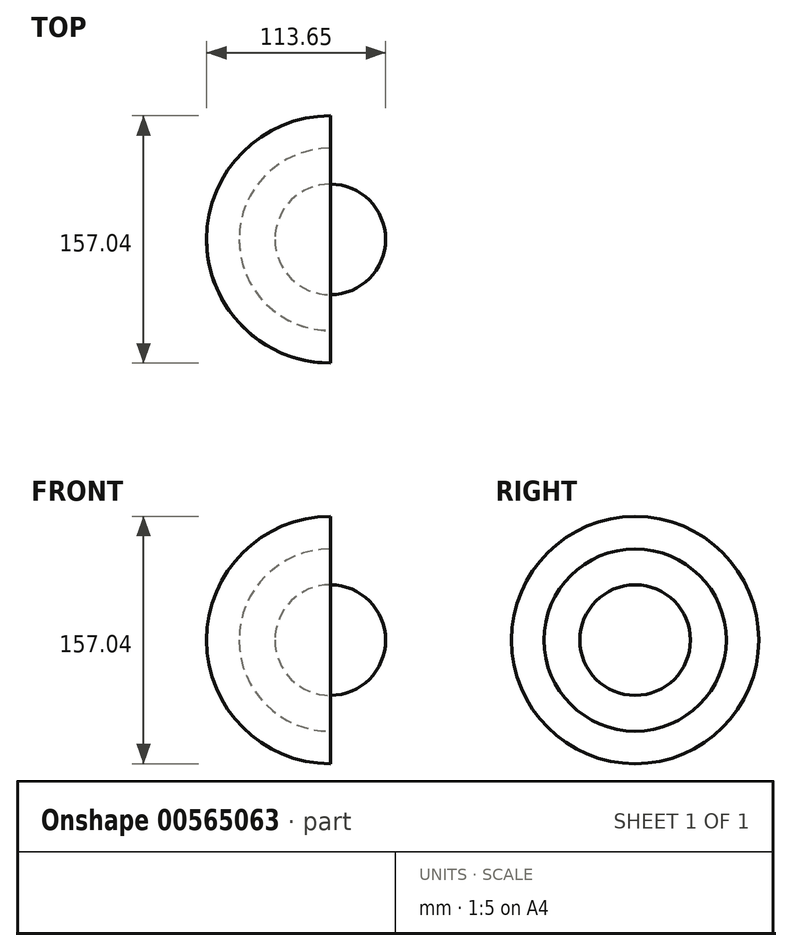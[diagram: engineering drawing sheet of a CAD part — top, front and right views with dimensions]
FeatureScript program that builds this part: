
annotation { "Feature Type Name" : "Feature", "Feature Type Description" : "" }
export const myFeature = defineFeature(function(context is Context, id is Id, definition is map)
    precondition{}
    {
        {
            var Q0;
            Q0=qCreatedBy(makeId("Top.planeOp"),FACE);
            var sketch = newSketch(context, id + "F0", { "sketchPlane" : qUnion([Q0])});
            skCircle(sketch, "E0", {"center": v(0, 0) * mm, "radius": 35.13 * mm});
            skPoint(sketch, "E1", {"position": v(-35.13, 0) * mm});
            skLineSegment(sketch, "E2", {"start": v(-35.13, 0) * mm, "end": v(35.13, 0) * mm});
            skCircle(sketch, "E3", {"center": v(0, 0) * mm, "radius": 57.87 * mm});
            skLineSegment(sketch, "E4", {"start": v(-35.13, 0) * mm, "end": v(-57.87, 0) * mm});
            skLineSegment(sketch, "E5", {"start": v(35.13, 0) * mm, "end": v(57.87, 0) * mm});
            skLineSegment(sketch, "E6", {"start": v(-57.87, 0) * mm, "end": v(-78.52, 0) * mm});
            skCircle(sketch, "E7", {"center": v(0, 0) * mm, "radius": 78.52 * mm});
            skLineSegment(sketch, "E8", {"start": v(57.87, 0) * mm, "end": v(78.52, 0) * mm});
            skLineSegment(sketch, "E9", {"start": v(0, -78.52) * mm, "end": v(0, 78.52) * mm});
            skLineSegment(sketch, "E10.bottom", {"start": v(-254, 254) * mm, "end": v(254, 254) * mm});
            skLineSegment(sketch, "E10.top", {"start": v(-254, -254) * mm, "end": v(254, -254) * mm});
            skLineSegment(sketch, "E10.left", {"start": v(-254, 254) * mm, "end": v(-254, -254) * mm});
            skLineSegment(sketch, "E10.right", {"start": v(254, 254) * mm, "end": v(254, -254) * mm});
            skSolve(sketch);
        }
        {
            var Q0;
            {var subQ0=sQuery(id+"F0.wireOp",EDGE,"E2");Q0=makeQuery(id+"F0.imprint","IMPRINT",FACE,{"disambiguationData":[TD([[makeQuery(id+"F0.imprint","IMPRINT",EDGE,{"derivedFrom":subQ0}),-1.0]])]});}
            var Q1;
            Q1=sQuery(id+"F0.wireOp",EDGE,"E2");
            revolve(context, id + "F1", {"entities" : qUnion([Q0]), "axis" : qUnion([Q1]), "revolveType" : RevolveType.FULL});
        }
        {
            var Q0;
            {var subQ0=sQuery(id+"F0.wireOp",EDGE,"E6");Q0=makeQuery(id+"F0.imprint","IMPRINT",FACE,{"disambiguationData":[TD([[makeQuery(id+"F0.imprint","IMPRINT",EDGE,{"derivedFrom":subQ0}),1.0]])]});}
            var Q1;
            Q1=sQuery(id+"F0.wireOp",EDGE,"E2");
            revolve(context, id + "F2", {"entities" : qUnion([Q0]), "axis" : qUnion([Q1]), "revolveType" : RevolveType.ONE_DIRECTION, "oppositeDirection" : true, "angle" : 360 * degree});
        }
    });
